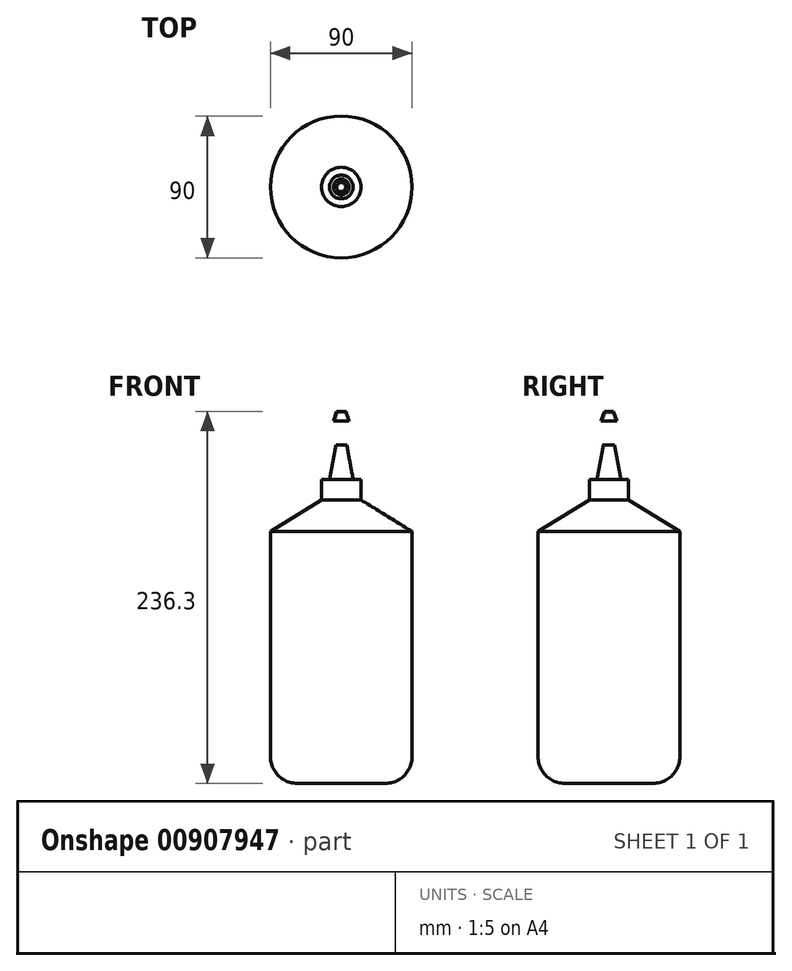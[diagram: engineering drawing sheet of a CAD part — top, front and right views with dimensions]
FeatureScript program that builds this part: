
annotation { "Feature Type Name" : "Feature", "Feature Type Description" : "" }
export const myFeature = defineFeature(function(context is Context, id is Id, definition is map)
    precondition{}
    {
        {
            var Q0;
            Q0=qCreatedBy(makeId("Top.planeOp"),FACE);
            var sketch = newSketch(context, id + "F0", { "sketchPlane" : qUnion([Q0])});
            skCircle(sketch, "E0", {"center": v(0, 0) * mm, "radius": 45 * mm});
            skSolve(sketch);
        }
        {
            var Q0;
            Q0=makeQuery(id+"F0.imprint","IMPRINT",FACE,{"disambiguationData":[TD([[makeQuery(id+"F0.imprint","IMPRINT",EDGE,{"derivedFrom":sQuery(id+"F0.wireOp",EDGE,"E0")}),1.0]])]});
            extrude(context, id + "F1", {"entities" : qUnion([Q0]), "depth" : 160 * mm, "offsetDistance" : 25 * mm});
        }
        {
            var Q0;
            Q0=makeQuery(id+"F1.opExtrude","CAP_EDGE",EDGE,{"disambiguationData":[OSD([sQuery(id+"F0.wireOp",EDGE,"E0")])],"isStart":true});
            fillet(context, id + "F2", {"entities" : qUnion([Q0]), "radius" : 17 * mm, "tangentPropagation" : true, "allowEdgeOverflow" : false});
        }
        {
            var Q0;
            Q0=makeQuery(id+"F1.opExtrude","CAP_FACE",FACE,{"disambiguationData":[OSD([sQuery(id+"F0.wireOp",EDGE,"E0")])],"isStart":false});
            cPlane(context, id + "F3", {"entities" : qUnion([Q0]), "cplaneType" : CPlaneType.OFFSET, "offset" : 20 * mm, "width" : 150 * mm, "height" : 150 * mm});
        }
        {
            var Q0;
            Q0=qCreatedBy(id+"F3.planeOp",FACE);
            var sketch = newSketch(context, id + "F4", { "sketchPlane" : qUnion([Q0])});
            skCircle(sketch, "E1", {"center": v(0, 0) * mm, "radius": 12.5 * mm});
            skSolve(sketch);
        }
        {
            var Q1;
            Q1=makeQuery(id+"F1.opExtrude","CAP_FACE",FACE,{"disambiguationData":[OSD([sQuery(id+"F0.wireOp",EDGE,"E0")])],"isStart":false});
            var Q2;
            Q2=makeQuery(id+"F4.imprint","IMPRINT",FACE,{"disambiguationData":[TD([[makeQuery(id+"F4.imprint","IMPRINT",EDGE,{"derivedFrom":sQuery(id+"F4.wireOp",EDGE,"E1")}),1.0]])]});
            loft(context, id + "F5", {"operationType" : NewBodyOperationType.ADD, "sheetProfilesArray" : [{ "sheetProfileEntities" : qUnion([Q1]) }, { "sheetProfileEntities" : qUnion([Q2]) }]});
        }
        {
            var Q0;
            Q0=makeQuery(id+"F5.opLoft","CAP_FACE",FACE,{"disambiguationData":[OSD([makeQuery(id+"F4.imprint","IMPRINT",FACE,{"disambiguationData":[TD([[makeQuery(id+"F4.imprint","IMPRINT",EDGE,{"derivedFrom":sQuery(id+"F4.wireOp",EDGE,"E1")}),1.0]])]})])],"isStart":true});
            extrude(context, id + "F6", {"entities" : qUnion([Q0]), "operationType" : NewBodyOperationType.ADD, "depth" : 13 * mm, "offsetDistance" : 25 * mm});
        }
        {
            var Q0;
            Q0=makeQuery(id+"F6.opExtrude","CAP_FACE",FACE,{"disambiguationData":[OSD([makeQuery(id+"F4.imprint","IMPRINT",FACE,{"disambiguationData":[TD([[makeQuery(id+"F4.imprint","IMPRINT",EDGE,{"derivedFrom":sQuery(id+"F4.wireOp",EDGE,"E1")}),1.0]])]})])],"isStart":false});
            var sketch = newSketch(context, id + "F7", { "sketchPlane" : qUnion([Q0])});
            skCircle(sketch, "E2", {"center": v(0, 0) * mm, "radius": 7.5 * mm});
            skSolve(sketch);
        }
        {
            var Q0;
            Q0=qCreatedBy(id+"F3.planeOp",FACE);
            cPlane(context, id + "F8", {"entities" : qUnion([Q0]), "cplaneType" : CPlaneType.OFFSET, "offset" : 35 * mm, "width" : 150 * mm, "height" : 150 * mm});
        }
        {
            var Q0;
            Q0=qCreatedBy(id+"F8.planeOp",FACE);
            var sketch = newSketch(context, id + "F9", { "sketchPlane" : qUnion([Q0])});
            skCircle(sketch, "E3", {"center": v(0, 0) * mm, "radius": 3.5 * mm});
            skSolve(sketch);
        }
        {
            var Q1;
            Q1=makeQuery(id+"F9.imprint","IMPRINT",FACE,{"disambiguationData":[TD([[makeQuery(id+"F9.imprint","IMPRINT",EDGE,{"derivedFrom":sQuery(id+"F9.wireOp",EDGE,"E3")}),1.0]])]});
            var Q2;
            Q2=makeQuery(id+"F7.imprint","IMPRINT",FACE,{"disambiguationData":[TD([[makeQuery(id+"F7.imprint","IMPRINT",EDGE,{"derivedFrom":sQuery(id+"F7.wireOp",EDGE,"E2")}),1.0]])]});
            loft(context, id + "F10", {"operationType" : NewBodyOperationType.ADD, "sheetProfilesArray" : [{ "sheetProfileEntities" : qUnion([Q1]) }, { "sheetProfileEntities" : qUnion([Q2]) }]});
        }
        {
            var Q0;
            Q0=qCreatedBy(id+"F8.planeOp",FACE);
            cPlane(context, id + "F11", {"entities" : qUnion([Q0]), "cplaneType" : CPlaneType.OFFSET, "offset" : 15.3 * mm, "width" : 150 * mm, "height" : 150 * mm});
        }
        {
            var Q0;
            Q0=qCreatedBy(id+"F11.planeOp",FACE);
            var sketch = newSketch(context, id + "F12", { "sketchPlane" : qUnion([Q0])});
            skCircle(sketch, "E4", {"center": v(0, 0) * mm, "radius": 5.04 * mm});
            skSolve(sketch);
        }
        {
            var Q0;
            Q0=qCreatedBy(id+"F11.planeOp",FACE);
            cPlane(context, id + "F13", {"entities" : qUnion([Q0]), "cplaneType" : CPlaneType.OFFSET, "offset" : 6 * mm, "width" : 150 * mm, "height" : 150 * mm});
        }
        {
            var Q0;
            Q0=qCreatedBy(id+"F13.planeOp",FACE);
            var sketch = newSketch(context, id + "F14", { "sketchPlane" : qUnion([Q0])});
            skCircle(sketch, "E5", {"center": v(0, 0) * mm, "radius": 3 * mm});
            skSolve(sketch);
        }
        {
            var Q0;
            Q0 = qSketchRegion(id + "F14", true);
            var Q1;
            Q1 = qSketchRegion(id + "F12", true);
            loft(context, id + "F15", {"sheetProfilesArray" : [{ "sheetProfileEntities" : qUnion([Q0]) }, { "sheetProfileEntities" : qUnion([Q1]) }]});
        }
        {
            var Q0;
            Q0=makeQuery(id+"F15.opLoft","CAP_FACE",FACE,{"disambiguationData":[OSD([makeQuery(id+"F12.imprint","IMPRINT",FACE,{"disambiguationData":[TD([[makeQuery(id+"F12.imprint","IMPRINT",EDGE,{"derivedFrom":sQuery(id+"F12.wireOp",EDGE,"E4")}),1.0]])]})])],"isStart":true});
            shell(context, id + "F16", {"entities" : qUnion([Q0]), "thickness" : 1 * mm});
        }
        {
            var Q0;
            Q0=qCreatedBy(makeId("Right.planeOp"),FACE);
            var sketch = newSketch(context, id + "F17", { "sketchPlane" : qUnion([Q0])});
            skFitSpline(sketch, "E6", {"points": [v(0, 190.48) * mm, v(33.36, 197.98) * mm, v(24.36, 221.97) * mm, v(0, 232.46) * mm], "startDerivative": vector(122.45, 1.74) * mm, "endDerivative": vector(-81.2, 17.67) * mm});
            skSolve(sketch);
        }
        {
            var Q0;
            Q0=qCreatedBy(makeId("Front.planeOp"),FACE);
            var sketch = newSketch(context, id + "F18", { "sketchPlane" : qUnion([Q0])});
            skLineSegment(sketch, "E7.bottom", {"start": v(-1, 189.48) * mm, "end": v(1, 189.48) * mm});
            skLineSegment(sketch, "E7.top", {"start": v(-1, 191.48) * mm, "end": v(1, 191.48) * mm});
            skLineSegment(sketch, "E7.left", {"start": v(-1, 189.48) * mm, "end": v(-1, 191.48) * mm});
            skLineSegment(sketch, "E7.right", {"start": v(1, 189.48) * mm, "end": v(1, 191.48) * mm});
            skPoint(sketch, "E7.middle", {"position": v(0, 190.48) * mm});
            skSolve(sketch);
        }
    });
